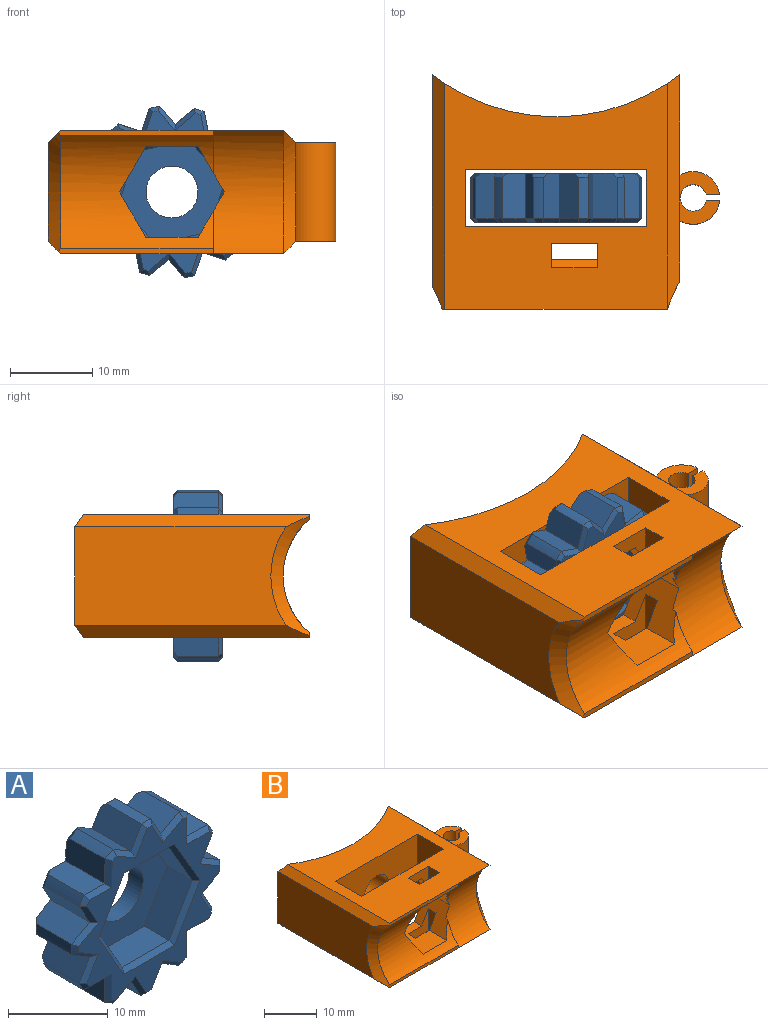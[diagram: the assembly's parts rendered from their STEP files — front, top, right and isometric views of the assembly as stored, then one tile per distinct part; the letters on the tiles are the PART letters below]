
ASSEMBLY  parts=2 mates=1
PART A: 100 faces, bbox 21x6x21 mm
  f0: plane 5.7x3.5mm, normal (0.87,0,-0.5), area 23mm2, adj f1,f41,f45,f84
  f1: plane 6.58x3.5mm, normal (0,0,-1), area 23mm2, adj f0,f2,f45,f86
  f2: plane 5.7x3.5mm, normal (-0.87,0,-0.5), area 23mm2, adj f1,f3,f45,f87
  f3: plane 5.7x3.5mm, normal (-0.87,0,0.5), area 23mm2, adj f2,f4,f45,f85
  f4: plane 6.58x3.5mm, normal (0,0,1), area 23mm2, adj f3,f41,f45,f83
  f5: plane 5.51x2.63mm, normal (-0.87,0,-0.48), area 16.3mm2, adj f6,f40,f43,f78,f92
  f6: plane 5.51x2.56mm, normal (-0.48,0,0.87), area 15.9mm2, adj f5,f7,f43,f76,f91
  f7: cylinder r=10.5mm len=5mm, axis (0,1,0), area 6.4mm2, adj f6,f8,f74,f91
  f8: plane 5.51x2.57mm, normal (-0.52,0,-0.86), area 16.3mm2, adj f7,f9,f43,f72,f91
  f9: plane 5.51x2.51mm, normal (-0.86,0,0.52), area 15.9mm2, adj f8,f10,f43,f70,f90
  f10: cylinder r=10.5mm len=5mm, axis (0,1,0), area 6.4mm2, adj f9,f11,f68,f90
  f11: plane 5.51x3mm, normal (-0.02,0,-1), area 16.3mm2, adj f10,f12,f43,f66,f90
  f12: plane 5.51x2.93mm, normal (-1,0,0.02), area 15.9mm2, adj f11,f13,f43,f64,f89
  f13: cylinder r=10.5mm len=5mm, axis (0,1,0), area 6.4mm2, adj f12,f14,f62,f89
  f14: plane 5.51x2.63mm, normal (0.48,0,-0.87), area 16.3mm2, adj f13,f15,f43,f60,f89
  f15: plane 5.51x2.56mm, normal (-0.87,0,-0.48), area 15.9mm2, adj f14,f16,f43,f58,f88
  f16: cylinder r=10.5mm len=5mm, axis (0,1,0), area 6.4mm2, adj f15,f17,f56,f88
  f17: plane 5.51x2.57mm, normal (0.86,0,-0.52), area 16.3mm2, adj f16,f18,f43,f54,f88
  f18: plane 5.51x2.51mm, normal (-0.52,0,-0.86), area 15.9mm2, adj f17,f19,f43,f52,f99
  f19: cylinder r=10.5mm len=5mm, axis (0,1,0), area 6.4mm2, adj f18,f20,f50,f99
  f20: plane 5.51x3mm, normal (1,0,-0.02), area 16.3mm2, adj f19,f21,f43,f48,f99
  f21: plane 5.51x2.93mm, normal (-0.02,0,-1), area 15.9mm2, adj f20,f22,f43,f46,f98
  f22: cylinder r=10.5mm len=5mm, axis (0,1,0), area 6.4mm2, adj f21,f23,f47,f98
  f23: plane 5.51x2.63mm, normal (0.87,0,0.48), area 16.3mm2, adj f22,f24,f43,f49,f98
  f24: plane 5.51x2.56mm, normal (0.48,0,-0.87), area 15.9mm2, adj f23,f25,f43,f51,f97
  f25: cylinder r=10.5mm len=5mm, axis (0,1,0), area 6.4mm2, adj f24,f26,f53,f97
  f26: plane 5.51x2.57mm, normal (0.52,0,0.86), area 16.3mm2, adj f25,f27,f43,f55,f97
  f27: plane 5.51x2.51mm, normal (0.86,0,-0.52), area 15.9mm2, adj f26,f28,f43,f57,f96
  f28: cylinder r=10.5mm len=5mm, axis (0,1,0), area 6.4mm2, adj f27,f29,f59,f96
  f29: plane 5.51x3mm, normal (0.02,0,1), area 16.3mm2, adj f28,f30,f43,f61,f96
  f30: plane 5.51x2.93mm, normal (1,0,-0.02), area 15.9mm2, adj f29,f31,f43,f63,f95
  f31: cylinder r=10.5mm len=5mm, axis (0,1,0), area 6.4mm2, adj f30,f32,f65,f95
  f32: plane 5.51x2.63mm, normal (-0.48,0,0.87), area 16.3mm2, adj f31,f33,f43,f67,f95
  f33: plane 5.51x2.56mm, normal (0.87,0,0.48), area 15.9mm2, adj f32,f34,f43,f69,f94
  f34: cylinder r=10.5mm len=5mm, axis (0,1,0), area 6.4mm2, adj f33,f35,f71,f94
  f35: plane 5.51x2.57mm, normal (-0.86,0,0.52), area 16.3mm2, adj f34,f36,f43,f73,f94
  f36: plane 5.51x2.51mm, normal (0.52,0,0.86), area 15.9mm2, adj f35,f37,f43,f75,f93
  f37: cylinder r=10.5mm len=5mm, axis (0,1,0), area 6.4mm2, adj f36,f38,f77,f93
  f38: plane 5.51x3mm, normal (-1,0,0.02), area 16.3mm2, adj f37,f39,f43,f79,f93
  f39: plane 5.51x2.93mm, normal (0.02,0,1), area 15.9mm2, adj f38,f40,f43,f81,f92
  f40: cylinder r=10.5mm len=5mm, axis (0,1,0), area 6.4mm2, adj f5,f39,f80,f92
  f41: plane 5.7x3.5mm, normal (0.87,0,0.5), area 23mm2, adj f0,f4,f45,f82
  f42: plane 20x20mm, normal (0,-1,0), area 110.9mm2, adj f46,f47,f48,f49,f50,f51,f52,f53
  f43: plane 20x20mm, normal (0,1,0), area 246.2mm2, adj f5,f6,f8,f9,f11,f12,f14,f15
  f44: cylinder r=3.15mm len=6.3mm, axis (0,1,0), area 39.6mm2, adj f43,f45
  f45: plane 13.16x11.4mm, normal (0,-1,0), area 81.4mm2, adj f0,f1,f2,f3,f4,f41,f44
  f46: plane 3.42x0.57mm, normal (-0.01,-0.71,-0.71), area 2.1mm2, adj f21,f42,f47,f48
  f47: cone r=10mm half-angle=45deg, axis (0,1,0), area 0.7mm2, adj f22,f42,f46,f49
  f48: plane 3.5x0.55mm, normal (0.71,-0.71,-0.01), area 2.2mm2, adj f20,f42,f46,f50
  f49: plane 2.82x2.13mm, normal (0.62,-0.71,0.34), area 2.2mm2, adj f23,f42,f47,f51
  f50: cone r=10mm half-angle=45deg, axis (0,1,0), area 0.7mm2, adj f19,f42,f48,f52
  f51: plane 3.24x1.72mm, normal (0.34,-0.71,-0.62), area 2.1mm2, adj f24,f42,f49,f53
  f52: plane 2.7x2.2mm, normal (-0.36,-0.71,-0.61), area 2.1mm2, adj f18,f42,f50,f54
  f53: cone r=10mm half-angle=45deg, axis (0,1,0), area 0.7mm2, adj f25,f42,f51,f55
  f54: plane 3.25x1.84mm, normal (0.61,-0.71,-0.36), area 2.2mm2, adj f17,f42,f52,f56
  f55: plane 3.25x1.84mm, normal (0.36,-0.71,0.61), area 2.2mm2, adj f26,f42,f53,f57
  f56: cone r=10mm half-angle=45deg, axis (0,1,0), area 0.7mm2, adj f16,f42,f54,f58
  f57: plane 2.7x2.2mm, normal (0.61,-0.71,-0.36), area 2.1mm2, adj f27,f42,f55,f59
  f58: plane 3.24x1.72mm, normal (-0.62,-0.71,-0.34), area 2.1mm2, adj f15,f42,f56,f60
  f59: cone r=10mm half-angle=45deg, axis (0,1,0), area 0.7mm2, adj f28,f42,f57,f61
  f60: plane 2.82x2.13mm, normal (0.34,-0.71,-0.62), area 2.2mm2, adj f14,f42,f58,f62
  f61: plane 3.5x0.55mm, normal (0.01,-0.71,0.71), area 2.2mm2, adj f29,f42,f59,f63
  f62: cone r=10mm half-angle=45deg, axis (0,1,0), area 0.7mm2, adj f13,f42,f60,f64
  f63: plane 3.42x0.57mm, normal (0.71,-0.71,-0.01), area 2.1mm2, adj f30,f42,f61,f65
  f64: plane 3.42x0.57mm, normal (-0.71,-0.71,0.01), area 2.1mm2, adj f12,f42,f62,f66
  f65: cone r=10mm half-angle=45deg, axis (0,1,0), area 0.7mm2, adj f31,f42,f63,f67
  f66: plane 3.5x0.55mm, normal (-0.01,-0.71,-0.71), area 2.2mm2, adj f11,f42,f64,f68
  f67: plane 2.82x2.13mm, normal (-0.34,-0.71,0.62), area 2.2mm2, adj f32,f42,f65,f69
  f68: cone r=10mm half-angle=45deg, axis (0,1,0), area 0.7mm2, adj f10,f42,f66,f70
  f69: plane 3.24x1.72mm, normal (0.62,-0.71,0.34), area 2.1mm2, adj f33,f42,f67,f71
  f70: plane 2.7x2.2mm, normal (-0.61,-0.71,0.36), area 2.1mm2, adj f9,f42,f68,f72
  f71: cone r=10mm half-angle=45deg, axis (0,1,0), area 0.7mm2, adj f34,f42,f69,f73
  f72: plane 3.25x1.84mm, normal (-0.36,-0.71,-0.61), area 2.2mm2, adj f8,f42,f70,f74
  f73: plane 3.25x1.84mm, normal (-0.61,-0.71,0.36), area 2.2mm2, adj f35,f42,f71,f75
  f74: cone r=10mm half-angle=45deg, axis (0,1,0), area 0.7mm2, adj f7,f42,f72,f76
  f75: plane 2.7x2.2mm, normal (0.36,-0.71,0.61), area 2.1mm2, adj f36,f42,f73,f77
  f76: plane 3.24x1.72mm, normal (-0.34,-0.71,0.62), area 2.1mm2, adj f6,f42,f74,f78
  f77: cone r=10mm half-angle=45deg, axis (0,1,0), area 0.7mm2, adj f37,f42,f75,f79
  f78: plane 2.82x2.13mm, normal (-0.62,-0.71,-0.34), area 2.2mm2, adj f5,f42,f76,f80
  f79: plane 3.5x0.55mm, normal (-0.71,-0.71,0.01), area 2.2mm2, adj f38,f42,f77,f81
  f80: cone r=10mm half-angle=45deg, axis (0,1,0), area 0.7mm2, adj f40,f42,f78,f81
  f81: plane 3.42x0.57mm, normal (0.01,-0.71,0.71), area 2.1mm2, adj f39,f42,f79,f80
  f82: plane 6.2x3.87mm, normal (0.61,-0.71,0.35), area 4.9mm2, adj f41,f42,f83,f84
  f83: plane 7.16x0.5mm, normal (0,-0.71,0.71), area 4.9mm2, adj f4,f42,f82,f85
  f84: plane 6.2x3.87mm, normal (0.61,-0.71,-0.35), area 4.9mm2, adj f0,f42,f82,f86
  f85: plane 6.2x3.87mm, normal (-0.61,-0.71,0.35), area 4.9mm2, adj f3,f42,f83,f87
  f86: plane 7.16x0.5mm, normal (0,-0.71,-0.71), area 4.9mm2, adj f1,f42,f84,f87
  f87: plane 6.2x3.87mm, normal (-0.61,-0.71,-0.35), area 4.9mm2, adj f2,f42,f85,f86
  f88: cone r=10.5mm half-angle=45deg, axis (0,-1,0), area 1.1mm2, adj f15,f16,f17,f43
  f89: cone r=10.5mm half-angle=45deg, axis (0,-1,0), area 1.1mm2, adj f12,f13,f14,f43
  f90: cone r=10.5mm half-angle=45deg, axis (0,-1,0), area 1.1mm2, adj f9,f10,f11,f43
  f91: cone r=10.5mm half-angle=45deg, axis (0,-1,0), area 1.1mm2, adj f6,f7,f8,f43
  f92: cone r=10.5mm half-angle=45deg, axis (0,-1,0), area 1.1mm2, adj f5,f39,f40,f43
  f93: cone r=10.5mm half-angle=45deg, axis (0,-1,0), area 1.1mm2, adj f36,f37,f38,f43
  f94: cone r=10.5mm half-angle=45deg, axis (0,-1,0), area 1.1mm2, adj f33,f34,f35,f43
  f95: cone r=10.5mm half-angle=45deg, axis (0,-1,0), area 1.1mm2, adj f30,f31,f32,f43
  f96: cone r=10.5mm half-angle=45deg, axis (0,-1,0), area 1.1mm2, adj f27,f28,f29,f43
  f97: cone r=10.5mm half-angle=45deg, axis (0,-1,0), area 1.1mm2, adj f24,f25,f26,f43
  f98: cone r=10.5mm half-angle=45deg, axis (0,-1,0), area 1.1mm2, adj f21,f22,f23,f43
  f99: cone r=10.5mm half-angle=45deg, axis (0,-1,0), area 1.1mm2, adj f18,f19,f20,f43
PART B: 46 faces, bbox 35x28.7x17.5 mm
  f0: plane 12.23x12mm, normal (1,0,0), area 146.8mm2, adj f11,f31,f32,f39
  f1: plane 8.8x5.59mm, normal (-0.87,0,-0.5), area 38.5mm2, adj f2,f4,f13,f19,f20,f21,f28,f29
  f2: plane 8.71x6.35mm, normal (0,0,-1), area 47.9mm2, adj f1,f13,f16,f19,f27,f28,f30
  f3: plane 8.71x6.35mm, normal (0,0,1), area 47.9mm2, adj f4,f13,f17,f19,f23,f25,f26
  f4: plane 8.8x5.59mm, normal (-0.87,0,0.5), area 38.5mm2, adj f1,f3,f13,f19,f20,f22,f23,f24
  f5: plane 18.78x0.65mm, normal (0,-1,0), area 12mm2, adj f15,f19,f22,f34,f36
  f6: plane 18.78x0.65mm, normal (0,-1,0), area 12mm2, adj f14,f19,f21,f35,f36
  f7: plane 12x7.39mm, normal (1,0,0), area 74.1mm2, adj f31,f32,f33,f40
  f8: plane 15x7mm, normal (1,0,0), area 105mm2, adj f9,f13,f14,f15
  f9: plane 22x15mm, normal (0,-1,0), area 296.8mm2, adj f8,f10,f14,f15,f18
  f10: plane 15x7mm, normal (-1,0,0), area 105mm2, adj f9,f13,f14,f15
  f11: cylinder r=24.5mm len=30mm, axis (0,0,-1), area 445.5mm2, adj f0,f12,f14,f15,f18,f31,f32,f34
  f12: plane 25.67x12mm, normal (-1,0,0), area 292.7mm2, adj f11,f34,f35,f36
  f13: plane 22x15mm, normal (0,1,0), area 225.2mm2, adj f1,f2,f3,f4,f8,f10,f14,f15
  f14: plane 27.39x27mm, normal (0,0,1), area 494.6mm2, adj f6,f8,f9,f10,f11,f13,f20,f27
  f15: plane 27.39x27mm, normal (0,0,-1), area 494.6mm2, adj f5,f8,f9,f10,f11,f13,f20,f23
  f16: plane 8.71x5.5mm, normal (0.87,0,-0.5), area 47.2mm2, adj f2,f13,f17,f19
  f17: plane 8.71x5.5mm, normal (0.87,0,0.5), area 47.2mm2, adj f3,f13,f16,f19
  f18: cylinder r=3.25mm len=6.55mm, axis (0,-1,0), area 131.5mm2, adj f9,f11
  f19: cylinder r=9mm len=18.5mm, axis (1,0,0), area 180mm2, adj f1,f2,f3,f4,f5,f6,f16,f17
  f20: cylinder r=9.5mm len=15mm, axis (1,0,0), area 143.8mm2, adj f1,f4,f14,f15,f21,f22,f33
  f21: plane 5.16x3.38mm, normal (1,0,0), area 2.9mm2, adj f1,f6,f19,f20
  f22: plane 5.16x3.38mm, normal (1,0,0), area 2.9mm2, adj f4,f5,f19,f20
  f23: plane 5.5x5.16mm, normal (0,-1,0), area 13.9mm2, adj f3,f4,f15,f24,f26
  f24: plane 5.16x3mm, normal (-1,0,0), area 10.8mm2, adj f4,f15,f23,f25,f37
  f25: plane 5.5x4.16mm, normal (0,1,0), area 8.4mm2, adj f3,f4,f24,f26,f37
  f26: plane 3x2mm, normal (1,0,0), area 4.5mm2, adj f3,f15,f23,f25,f37
  f27: plane 3x2mm, normal (1,0,0), area 4.5mm2, adj f2,f14,f28,f30,f38
  f28: plane 5.5x4.16mm, normal (0,1,0), area 8.4mm2, adj f1,f2,f27,f29,f38
  f29: plane 5.16x3mm, normal (-1,0,0), area 10.8mm2, adj f1,f14,f28,f30,f38
  f30: plane 5.5x5.16mm, normal (0,-1,0), area 13.9mm2, adj f1,f2,f14,f27,f29
  f31: plane 28.48x1.52mm, normal (0.71,0,-0.71), area 55.3mm2, adj f0,f7,f11,f15,f33,f41
  f32: plane 28.48x1.52mm, normal (0.71,0,0.71), area 55.3mm2, adj f0,f7,f11,f14,f33,f45
  f33: cone r=9.5mm half-angle=45deg, axis (1,0,0), area 31.4mm2, adj f7,f20,f31,f32
  f34: plane 28.48x1.52mm, normal (-0.71,0,-0.71), area 56.6mm2, adj f5,f11,f12,f15,f36
  f35: plane 28.48x1.52mm, normal (-0.71,0,0.71), area 56.6mm2, adj f6,f11,f12,f14,f36
  f36: cone r=10.5mm half-angle=45deg, axis (-1,0,0), area 31.4mm2, adj f5,f6,f12,f19,f34,f35
  f37: plane 5.5x1mm, normal (0,0.71,-0.71), area 7.8mm2, adj f15,f24,f25,f26
  f38: plane 5.5x1mm, normal (0,0.71,0.71), area 7.8mm2, adj f14,f27,f28,f29
  f39: cylinder r=3.2mm len=12mm, axis (0,0,1), area 76.3mm2, adj f0,f41,f42,f45
  f40: cylinder r=3.2mm len=12mm, axis (0,0,1), area 77.9mm2, adj f7,f41,f44,f45
  f41: plane 6.4x4.86mm, normal (0,0,-1), area 17.1mm2, adj f31,f39,f40,f42,f43,f44
  f42: plane 12x1.63mm, normal (0,-1,0), area 19.6mm2, adj f39,f41,f43,f45
  f43: cylinder r=1.6mm len=12mm, axis (0,0,1), area 111.7mm2, adj f41,f42,f44,f45
  f44: plane 12x1.61mm, normal (0,1,0), area 19.4mm2, adj f40,f41,f43,f45
  f45: plane 6.4x4.86mm, normal (0,0,1), area 17.1mm2, adj f32,f39,f40,f42,f43,f44
PLACE A rot(axis=(0,1,0),108.1deg) t=(-34.54,-12.36,-64.47)mm
PLACE B t=(-16.52,18.97,-16.71)mm fixed
MATE revolute A.f44 <-> B.f18  axis (0,1,0) through (-16.52,-12.36,-9.21)mm
